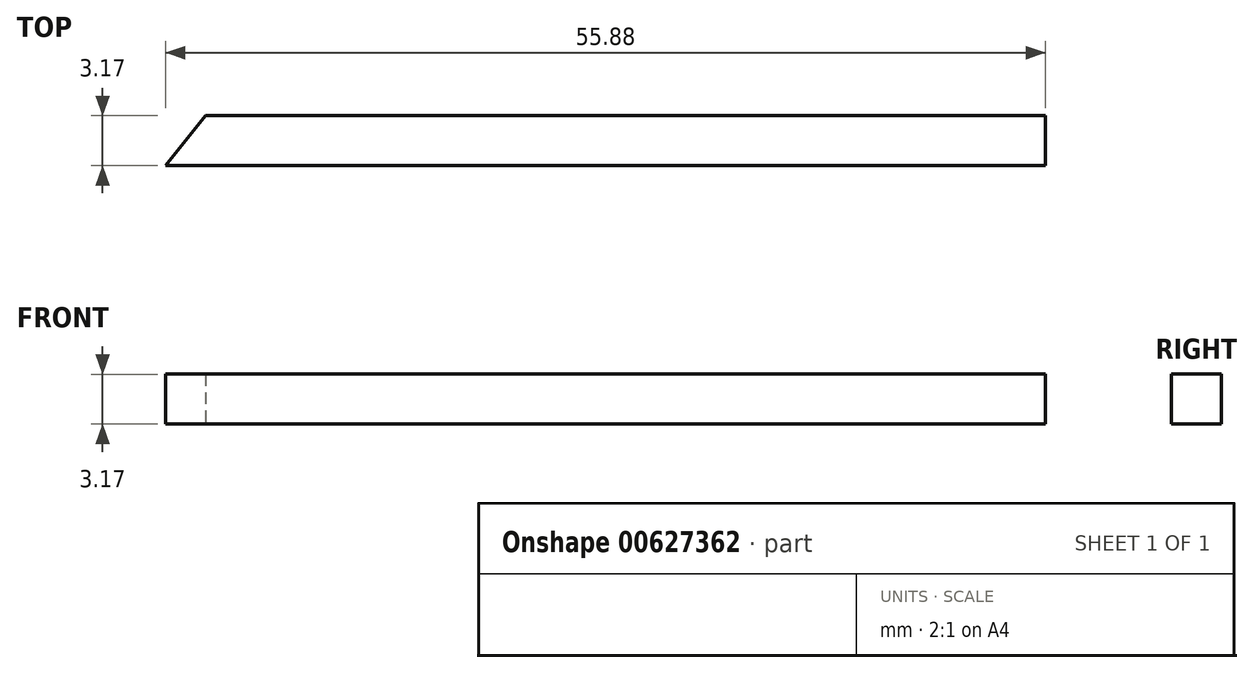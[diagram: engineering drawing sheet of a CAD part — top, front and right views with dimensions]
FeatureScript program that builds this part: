
annotation { "Feature Type Name" : "Feature", "Feature Type Description" : "" }
export const myFeature = defineFeature(function(context is Context, id is Id, definition is map)
    precondition{}
    {
        {
            var Q0;
            Q0=qCreatedBy(makeId("Top.planeOp"),FACE);
            var sketch = newSketch(context, id + "F0", { "sketchPlane" : qUnion([Q0])});
            skLineSegment(sketch, "E0", {"start": v(-89.33, -7.84) * mm, "end": v(-36, -7.84) * mm});
            skLineSegment(sketch, "E1", {"start": v(-36, -7.84) * mm, "end": v(-36, -11.01) * mm});
            skLineSegment(sketch, "E2", {"start": v(-36, -11.01) * mm, "end": v(-91.87, -11.01) * mm});
            skLineSegment(sketch, "E3", {"start": v(-91.87, -11.01) * mm, "end": v(-89.33, -7.84) * mm});
            skSolve(sketch);
        }
        {
            var Q0;
            Q0=makeQuery(id+"F0.imprint","IMPRINT",FACE,{"disambiguationData":[TD([[makeQuery(id+"F0.imprint","IMPRINT",EDGE,{"derivedFrom":sQuery(id+"F0.wireOp",EDGE,"E0")}),-1.0]])]});
            extrude(context, id + "F1", {"entities" : qUnion([Q0]), "depth" : 3.17 * mm, "offsetDistance" : 25.4 * mm});
        }
    });
